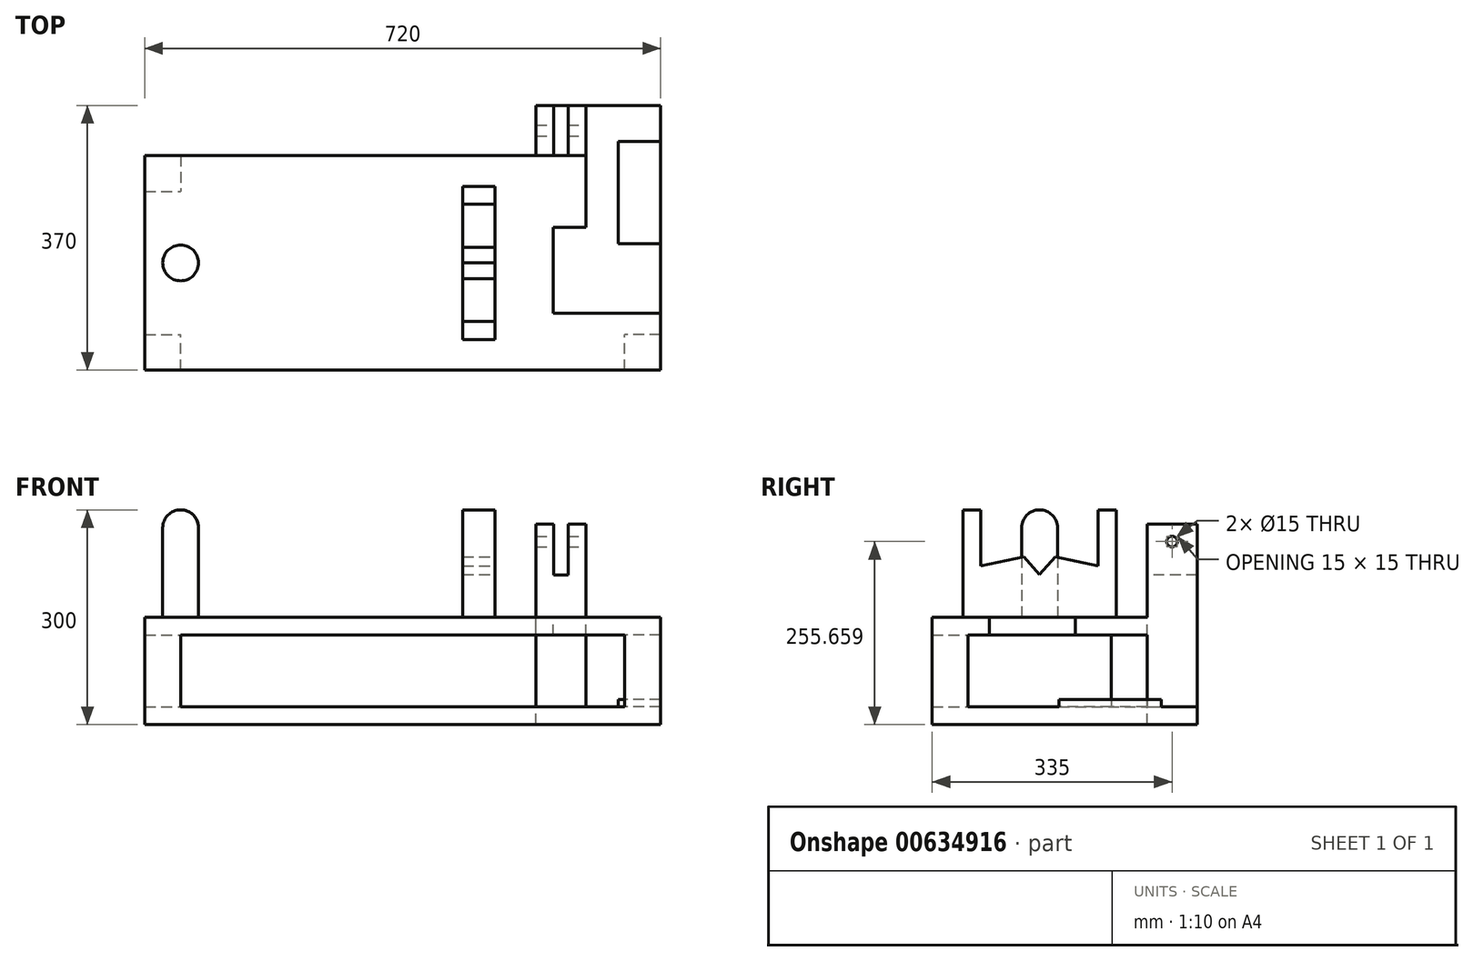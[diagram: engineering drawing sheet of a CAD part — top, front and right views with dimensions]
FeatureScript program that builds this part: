
annotation { "Feature Type Name" : "Feature", "Feature Type Description" : "" }
export const myFeature = defineFeature(function(context is Context, id is Id, definition is map)
    precondition{}
    {
        {
            var Q0;
            Q0=qCreatedBy(makeId("Top.planeOp"),FACE);
            var sketch = newSketch(context, id + "F0", { "sketchPlane" : qUnion([Q0])});
            skLineSegment(sketch, "E0.bottom", {"start": v(-360, 150) * mm, "end": v(360, 150) * mm});
            skLineSegment(sketch, "E0.top", {"start": v(-360, -150) * mm, "end": v(360, -150) * mm});
            skLineSegment(sketch, "E0.left", {"start": v(-360, 150) * mm, "end": v(-360, -150) * mm});
            skLineSegment(sketch, "E0.right", {"start": v(360, 150) * mm, "end": v(360, -150) * mm});
            skSolve(sketch);
        }
        {
            var Q0;
            Q0=makeQuery(id+"F0.imprint","IMPRINT",FACE,{"disambiguationData":[TD([[makeQuery(id+"F0.imprint","IMPRINT",EDGE,{"derivedFrom":sQuery(id+"F0.wireOp",EDGE,"E0.bottom")}),-1.0]])]});
            extrude(context, id + "F1", {"entities" : qUnion([Q0]), "depth" : 25 * mm, "offsetDistance" : 25 * mm});
        }
        {
            var Q0;
            Q0=makeQuery(id+"F1.opExtrude","CAP_FACE",FACE,{"disambiguationData":[OSD([sQuery(id+"F0.wireOp",EDGE,"E0.bottom"),sQuery(id+"F0.wireOp",EDGE,"E0.top"),sQuery(id+"F0.wireOp",EDGE,"E0.left"),sQuery(id+"F0.wireOp",EDGE,"E0.right")])],"isStart":false});
            var sketch = newSketch(context, id + "F2", { "sketchPlane" : qUnion([Q0])});
            skLineSegment(sketch, "E1.bottom", {"start": v(-360, -150) * mm, "end": v(-310, -150) * mm});
            skLineSegment(sketch, "E1.top", {"start": v(-360, -100) * mm, "end": v(-310, -100) * mm});
            skLineSegment(sketch, "E1.left", {"start": v(-360, -150) * mm, "end": v(-360, -100) * mm});
            skLineSegment(sketch, "E1.right", {"start": v(-310, -150) * mm, "end": v(-310, -100) * mm});
            skSolve(sketch);
        }
        {
            var Q0;
            Q0=makeQuery(id+"F2.imprint","IMPRINT",FACE,{"disambiguationData":[TD([[makeQuery(id+"F2.imprint","IMPRINT",EDGE,{"derivedFrom":sQuery(id+"F2.wireOp",EDGE,"E1.bottom")}),1.0]])]});
            extrude(context, id + "F3", {"entities" : qUnion([Q0]), "operationType" : NewBodyOperationType.ADD, "depth" : 100 * mm, "offsetDistance" : 25 * mm});
        }
        {
            var Q0;
            Q0=makeQuery(id+"F1.opExtrude","CAP_FACE",FACE,{"disambiguationData":[OSD([sQuery(id+"F0.wireOp",EDGE,"E0.bottom"),sQuery(id+"F0.wireOp",EDGE,"E0.top"),sQuery(id+"F0.wireOp",EDGE,"E0.left"),sQuery(id+"F0.wireOp",EDGE,"E0.right")])],"isStart":false});
            var sketch = newSketch(context, id + "F4", { "sketchPlane" : qUnion([Q0])});
            skLineSegment(sketch, "E2.bottom", {"start": v(360, -150) * mm, "end": v(310, -150) * mm});
            skLineSegment(sketch, "E2.top", {"start": v(360, -100) * mm, "end": v(310, -100) * mm});
            skLineSegment(sketch, "E2.left", {"start": v(360, -150) * mm, "end": v(360, -100) * mm});
            skLineSegment(sketch, "E2.right", {"start": v(310, -150) * mm, "end": v(310, -100) * mm});
            skLineSegment(sketch, "E3.bottom", {"start": v(360, 150) * mm, "end": v(310, 150) * mm});
            skLineSegment(sketch, "E3.top", {"start": v(360, 100) * mm, "end": v(310, 100) * mm});
            skLineSegment(sketch, "E3.left", {"start": v(360, 150) * mm, "end": v(360, 100) * mm});
            skLineSegment(sketch, "E3.right", {"start": v(310, 150) * mm, "end": v(310, 100) * mm});
            skLineSegment(sketch, "E4.bottom", {"start": v(-360, 150) * mm, "end": v(-310, 150) * mm});
            skLineSegment(sketch, "E4.top", {"start": v(-360, 100) * mm, "end": v(-310, 100) * mm});
            skLineSegment(sketch, "E4.left", {"start": v(-360, 150) * mm, "end": v(-360, 100) * mm});
            skLineSegment(sketch, "E4.right", {"start": v(-310, 150) * mm, "end": v(-310, 100) * mm});
            skSolve(sketch);
        }
        {
            var Q0;
            Q0=makeQuery(id+"F4.imprint","IMPRINT",FACE,{"disambiguationData":[TD([[makeQuery(id+"F4.imprint","IMPRINT",EDGE,{"derivedFrom":sQuery(id+"F4.wireOp",EDGE,"E2.bottom")}),1.0]])]});
            var Q1;
            Q1=makeQuery(id+"F4.imprint","IMPRINT",FACE,{"disambiguationData":[TD([[makeQuery(id+"F4.imprint","IMPRINT",EDGE,{"derivedFrom":sQuery(id+"F4.wireOp",EDGE,"E4.bottom")}),-1.0]])]});
            var Q2;
            Q2=makeQuery(id+"F4.imprint","IMPRINT",FACE,{"disambiguationData":[TD([[makeQuery(id+"F4.imprint","IMPRINT",EDGE,{"derivedFrom":sQuery(id+"F4.wireOp",EDGE,"E3.bottom")}),-1.0]])]});
            extrude(context, id + "F5", {"entities" : qUnion([Q0, Q1, Q2]), "operationType" : NewBodyOperationType.ADD, "depth" : 100 * mm, "offsetDistance" : 25 * mm});
        }
        {
            var Q0;
            Q0=makeQuery(id+"F5.opExtrude","CAP_FACE",FACE,{"disambiguationData":[OSD([sQuery(id+"F4.wireOp",EDGE,"E4.bottom"),sQuery(id+"F4.wireOp",EDGE,"E4.top"),sQuery(id+"F4.wireOp",EDGE,"E4.left"),sQuery(id+"F4.wireOp",EDGE,"E4.right")])],"isStart":false});
            var sketch = newSketch(context, id + "F6", { "sketchPlane" : qUnion([Q0])});
            skLineSegment(sketch, "E5.bottom", {"start": v(-360, 150) * mm, "end": v(360, 150) * mm});
            skLineSegment(sketch, "E5.top", {"start": v(-360, -150) * mm, "end": v(360, -150) * mm});
            skLineSegment(sketch, "E5.left", {"start": v(-360, 150) * mm, "end": v(-360, -150) * mm});
            skLineSegment(sketch, "E5.right", {"start": v(360, 150) * mm, "end": v(360, -150) * mm});
            skSolve(sketch);
        }
        {
            var Q0;
            {var subQ4=makeQuery(id+"F5.opExtrude","CAP_EDGE",EDGE,{"disambiguationData":[OSD([sQuery(id+"F4.wireOp",EDGE,"E4.top")])],"isStart":false});Q0=makeQuery(id+"F6.imprint","IMPRINT",FACE,{"disambiguationData":[TD([[makeQuery(id+"F6.imprint","IMPRINT",EDGE,{"derivedFrom":subQ4}),1.0]])]});}
            var Q1;
            {var subQ3=sQuery(id+"F6.wireOp",EDGE,"E5.top");Q1=makeQuery(id+"F6.imprint","IMPRINT",FACE,{"disambiguationData":[TD([[makeQuery(id+"F6.imprint","IMPRINT",EDGE,{"derivedFrom":subQ3}),1.0]])]});}
            extrude(context, id + "F7", {"entities" : qUnion([Q0, Q1]), "operationType" : NewBodyOperationType.ADD, "depth" : 25 * mm, "offsetDistance" : 25 * mm});
        }
        {
            var Q0;
            Q0=makeQuery(id+"F7.opExtrude","CAP_FACE",FACE,{"disambiguationData":[OSD([sQuery(id+"F6.wireOp",EDGE,"E5.bottom"),sQuery(id+"F6.wireOp",EDGE,"E5.top"),sQuery(id+"F6.wireOp",EDGE,"E5.left"),sQuery(id+"F6.wireOp",EDGE,"E5.right")])],"isStart":false});
            var sketch = newSketch(context, id + "F8", { "sketchPlane" : qUnion([Q0])});
            skCircle(sketch, "E6", {"center": v(-310, 0) * mm, "radius": 25 * mm});
            skSolve(sketch);
        }
        {
            var Q0;
            Q0=makeQuery(id+"F8.imprint","IMPRINT",FACE,{"disambiguationData":[TD([[makeQuery(id+"F8.imprint","IMPRINT",EDGE,{"derivedFrom":sQuery(id+"F8.wireOp",EDGE,"E6")}),1.0]])]});
            extrude(context, id + "F9", {"entities" : qUnion([Q0]), "operationType" : NewBodyOperationType.ADD, "depth" : 150 * mm, "offsetDistance" : 25 * mm});
        }
        {
            var Q0;
            Q0=makeQuery(id+"F7.opExtrude","CAP_FACE",FACE,{"disambiguationData":[OSD([sQuery(id+"F6.wireOp",EDGE,"E5.bottom"),sQuery(id+"F6.wireOp",EDGE,"E5.top"),sQuery(id+"F6.wireOp",EDGE,"E5.left"),sQuery(id+"F6.wireOp",EDGE,"E5.right")])],"isStart":false});
            var sketch = newSketch(context, id + "F10", { "sketchPlane" : qUnion([Q0])});
            skLineSegment(sketch, "E7.bottom", {"start": v(84, 106.83) * mm, "end": v(129, 106.83) * mm});
            skLineSegment(sketch, "E7.top", {"start": v(84, -106.83) * mm, "end": v(129, -106.83) * mm});
            skLineSegment(sketch, "E7.left", {"start": v(84, 106.83) * mm, "end": v(84, -106.83) * mm});
            skLineSegment(sketch, "E7.right", {"start": v(129, 106.83) * mm, "end": v(129, -106.83) * mm});
            skLineSegment(sketch, "E8", {"start": v(-360, 0) * mm, "end": v(360, 0) * mm});
            skSolve(sketch);
        }
        {
            var Q0;
            {var subQ0=sQuery(id+"F10.wireOp",EDGE,"E7.top");Q0=makeQuery(id+"F10.imprint","IMPRINT",FACE,{"disambiguationData":[TD([[makeQuery(id+"F10.imprint","IMPRINT",EDGE,{"derivedFrom":subQ0}),1.0]])]});}
            var Q1;
            {var subQ0=sQuery(id+"F10.wireOp",EDGE,"E7.bottom");Q1=makeQuery(id+"F10.imprint","IMPRINT",FACE,{"disambiguationData":[TD([[makeQuery(id+"F10.imprint","IMPRINT",EDGE,{"derivedFrom":subQ0}),-1.0]])]});}
            extrude(context, id + "F11", {"entities" : qUnion([Q0, Q1]), "operationType" : NewBodyOperationType.ADD, "depth" : 150 * mm, "offsetDistance" : 25 * mm});
        }
        {
            var Q0;
            Q0=makeQuery(id+"F11.opExtrude","SWEPT_FACE",FACE,{"disambiguationData":[OSD([sQuery(id+"F10.wireOp",EDGE,"E7.right")])]});
            var sketch = newSketch(context, id + "F12", { "sketchPlane" : qUnion([Q0])});
            skLineSegment(sketch, "E9", {"start": v(-81.83, 300) * mm, "end": v(-81.83, 221.94) * mm});
            skLineSegment(sketch, "E10", {"start": v(-81.83, 221.94) * mm, "end": v(-21.83, 234.49) * mm});
            skLineSegment(sketch, "E11", {"start": v(-21.83, 234.49) * mm, "end": v(0, 209.4) * mm});
            skLineSegment(sketch, "E12", {"start": v(0, 209.4) * mm, "end": v(21.83, 234.49) * mm});
            skLineSegment(sketch, "E13", {"start": v(21.83, 234.49) * mm, "end": v(81.83, 221.94) * mm});
            skLineSegment(sketch, "E14", {"start": v(81.83, 221.94) * mm, "end": v(81.83, 300) * mm});
            skLineSegment(sketch, "E15", {"start": v(-81.83, 300) * mm, "end": v(81.83, 300) * mm});
            skSolve(sketch);
        }
        {
            var Q0;
            Q0=qSketchRegion(id+"F12",true);
            extrude(context, id + "F13", {"entities" : qUnion([Q0]), "operationType" : NewBodyOperationType.REMOVE, "oppositeDirection" : true, "depth" : 50 * mm, "offsetDistance" : 25 * mm});
        }
        {
            var Q0;
            Q0=makeQuery(id+"F7.opExtrude","CAP_FACE",FACE,{"disambiguationData":[OSD([sQuery(id+"F6.wireOp",EDGE,"E5.bottom"),sQuery(id+"F6.wireOp",EDGE,"E5.top"),sQuery(id+"F6.wireOp",EDGE,"E5.left"),sQuery(id+"F6.wireOp",EDGE,"E5.right")])],"isStart":false});
            var sketch = newSketch(context, id + "F14", { "sketchPlane" : qUnion([Q0])});
            skLineSegment(sketch, "E16.bottom", {"start": v(186, 150) * mm, "end": v(256, 150) * mm});
            skLineSegment(sketch, "E16.top", {"start": v(186, 220) * mm, "end": v(256, 220) * mm});
            skLineSegment(sketch, "E16.left", {"start": v(186, 150) * mm, "end": v(186, 220) * mm});
            skLineSegment(sketch, "E16.right", {"start": v(256, 150) * mm, "end": v(256, 220) * mm});
            skSolve(sketch);
        }
        {
            var Q0;
            Q0=qSketchRegion(id+"F14",true);
            extrude(context, id + "F15", {"entities" : qUnion([Q0]), "operationType" : NewBodyOperationType.ADD, "oppositeDirection" : true, "depth" : 150 * mm, "offsetDistance" : 25 * mm});
        }
        {
            var Q0;
            Q0=qSketchRegion(id+"F14",true);
            extrude(context, id + "F16", {"entities" : qUnion([Q0]), "operationType" : NewBodyOperationType.ADD, "depth" : 130 * mm, "offsetDistance" : 25 * mm});
        }
        {
            var Q0;
            Q0=makeQuery(id+"F9.opExtrude","CAP_FACE",FACE,{"disambiguationData":[OSD([sQuery(id+"F8.wireOp",EDGE,"E6")])],"isStart":false});
            fillet(context, id + "F17", {"entities" : qUnion([Q0]), "radius" : 25 * mm, "tangentPropagation" : true, "allowEdgeOverflow" : false});
        }
        {
            var Q0;
            Q0=makeQuery(id+"F15.boolean.opBoolean","MERGE",FACE,{"derivedFrom":[makeQuery(id+"F7.opExtrude","CAP_FACE",FACE,{"disambiguationData":[OSD([sQuery(id+"F6.wireOp",EDGE,"E5.bottom"),sQuery(id+"F6.wireOp",EDGE,"E5.top"),sQuery(id+"F6.wireOp",EDGE,"E5.left"),sQuery(id+"F6.wireOp",EDGE,"E5.right")])],"isStart":false}),makeQuery(id+"F15.opExtrude","CAP_FACE",FACE,{"disambiguationData":[OSD([sQuery(id+"F14.wireOp",EDGE,"E16.bottom"),sQuery(id+"F14.wireOp",EDGE,"E16.top"),sQuery(id+"F14.wireOp",EDGE,"E16.left"),sQuery(id+"F14.wireOp",EDGE,"E16.right")])],"isStart":true})]});
            var sketch = newSketch(context, id + "F18", { "sketchPlane" : qUnion([Q0])});
            skLineSegment(sketch, "E17.bottom", {"start": v(360, -70) * mm, "end": v(210, -70) * mm});
            skLineSegment(sketch, "E17.top", {"start": v(360, 50) * mm, "end": v(210, 50) * mm});
            skLineSegment(sketch, "E17.left", {"start": v(360, -70) * mm, "end": v(360, 50) * mm});
            skLineSegment(sketch, "E17.right", {"start": v(210, -70) * mm, "end": v(210, 50) * mm});
            skSolve(sketch);
        }
        {
            var Q0;
            Q0=qSketchRegion(id+"F18",true);
            extrude(context, id + "F19", {"entities" : qUnion([Q0]), "operationType" : NewBodyOperationType.REMOVE, "oppositeDirection" : true, "depth" : 25 * mm, "offsetDistance" : 25 * mm});
        }
        {
            var Q0;
            Q0=makeQuery(id+"F15.boolean.opBoolean","MERGE",FACE,{"derivedFrom":[makeQuery(id+"F7.opExtrude","CAP_FACE",FACE,{"disambiguationData":[OSD([sQuery(id+"F6.wireOp",EDGE,"E5.bottom"),sQuery(id+"F6.wireOp",EDGE,"E5.top"),sQuery(id+"F6.wireOp",EDGE,"E5.left"),sQuery(id+"F6.wireOp",EDGE,"E5.right")])],"isStart":false}),makeQuery(id+"F15.opExtrude","CAP_FACE",FACE,{"disambiguationData":[OSD([sQuery(id+"F14.wireOp",EDGE,"E16.bottom"),sQuery(id+"F14.wireOp",EDGE,"E16.top"),sQuery(id+"F14.wireOp",EDGE,"E16.left"),sQuery(id+"F14.wireOp",EDGE,"E16.right")])],"isStart":true})]});
            var sketch = newSketch(context, id + "F20", { "sketchPlane" : qUnion([Q0])});
            skLineSegment(sketch, "E18.bottom", {"start": v(360, 150) * mm, "end": v(256, 150) * mm});
            skLineSegment(sketch, "E18.top", {"start": v(360, 50) * mm, "end": v(256, 50) * mm});
            skLineSegment(sketch, "E18.left", {"start": v(360, 150) * mm, "end": v(360, 50) * mm});
            skLineSegment(sketch, "E18.right", {"start": v(256, 150) * mm, "end": v(256, 50) * mm});
            skSolve(sketch);
        }
        {
            var Q0;
            Q0=qSketchRegion(id+"F20",true);
            extrude(context, id + "F21", {"entities" : qUnion([Q0]), "operationType" : NewBodyOperationType.REMOVE, "oppositeDirection" : true, "depth" : 150 * mm, "offsetDistance" : 25 * mm});
        }
        {
            var Q0;
            Q0=makeQuery(id+"F1.opExtrude","CAP_FACE",FACE,{"disambiguationData":[OSD([sQuery(id+"F0.wireOp",EDGE,"E0.bottom"),sQuery(id+"F0.wireOp",EDGE,"E0.top"),sQuery(id+"F0.wireOp",EDGE,"E0.left"),sQuery(id+"F0.wireOp",EDGE,"E0.right")])],"isStart":false});
            var sketch = newSketch(context, id + "F22", { "sketchPlane" : qUnion([Q0])});
            skLineSegment(sketch, "E19.bottom", {"start": v(360, 50) * mm, "end": v(256, 50) * mm});
            skLineSegment(sketch, "E19.top", {"start": v(360, 220) * mm, "end": v(256, 220) * mm});
            skLineSegment(sketch, "E19.left", {"start": v(360, 50) * mm, "end": v(360, 220) * mm});
            skLineSegment(sketch, "E19.right", {"start": v(256, 50) * mm, "end": v(256, 220) * mm});
            skSolve(sketch);
        }
        {
            var Q0;
            Q0=qSketchRegion(id+"F22",true);
            extrude(context, id + "F23", {"entities" : qUnion([Q0]), "operationType" : NewBodyOperationType.ADD, "oppositeDirection" : true, "depth" : 25 * mm, "offsetDistance" : 25 * mm});
        }
        {
            var Q0;
            Q0=makeQuery(id+"F16.opExtrude","SWEPT_FACE",FACE,{"disambiguationData":[OSD([sQuery(id+"F14.wireOp",EDGE,"E16.bottom")])]});
            var sketch = newSketch(context, id + "F24", { "sketchPlane" : qUnion([Q0])});
            skLineSegment(sketch, "E20.bottom", {"start": v(211, 280) * mm, "end": v(231, 280) * mm});
            skLineSegment(sketch, "E20.top", {"start": v(211, 208.66) * mm, "end": v(231, 208.66) * mm});
            skLineSegment(sketch, "E20.left", {"start": v(211, 280) * mm, "end": v(211, 208.66) * mm});
            skLineSegment(sketch, "E20.right", {"start": v(231, 280) * mm, "end": v(231, 208.66) * mm});
            skSolve(sketch);
        }
        {
            var Q0;
            Q0 = qSketchRegion(id + "F24", true);
            extrude(context, id + "F25", {"entities" : qUnion([Q0]), "operationType" : NewBodyOperationType.REMOVE, "oppositeDirection" : true, "depth" : 80 * mm, "offsetDistance" : 25 * mm});
        }
        {
            var Q0;
            {var subQ0=sQuery(id+"F14.wireOp",EDGE,"E16.right");Q0=makeQuery(id+"F21.boolean.opBoolean","MERGE",FACE,{"derivedFrom":[makeQuery(id+"F16.boolean.opBoolean","MERGE",FACE,{"derivedFrom":[makeQuery(id+"F15.opExtrude","SWEPT_FACE",FACE,{"disambiguationData":[OSD([subQ0])]}),makeQuery(id+"F16.opExtrude","SWEPT_FACE",FACE,{"disambiguationData":[OSD([subQ0])]})]}),makeQuery(id+"F21.opExtrude","SWEPT_FACE",FACE,{"disambiguationData":[OSD([sQuery(id+"F20.wireOp",EDGE,"E18.right")])]})]});}
            var sketch = newSketch(context, id + "F26", { "sketchPlane" : qUnion([Q0])});
            skCircle(sketch, "E21", {"center": v(185, 255.66) * mm, "radius": 7.5 * mm});
            skPoint(sketch, "E21.centerSnap0", {"position": v(185, 280) * mm});
            skSolve(sketch);
        }
        {
            var Q0;
            Q0 = qSketchRegion(id + "F26", true);
            extrude(context, id + "F27", {"entities" : qUnion([Q0]), "operationType" : NewBodyOperationType.REMOVE, "endBound" : BoundingType.THROUGH_ALL, "oppositeDirection" : true, "depth" : 25 * mm, "offsetDistance" : 25 * mm});
        }
        {
            var Q0;
            Q0=makeQuery(id+"F23.boolean.opBoolean","MERGE",FACE,{"derivedFrom":[makeQuery(id+"F1.opExtrude","CAP_FACE",FACE,{"disambiguationData":[OSD([sQuery(id+"F0.wireOp",EDGE,"E0.bottom"),sQuery(id+"F0.wireOp",EDGE,"E0.top"),sQuery(id+"F0.wireOp",EDGE,"E0.left"),sQuery(id+"F0.wireOp",EDGE,"E0.right")])],"isStart":false}),makeQuery(id+"F23.opExtrude","CAP_FACE",FACE,{"disambiguationData":[OSD([sQuery(id+"F22.wireOp",EDGE,"E19.bottom"),sQuery(id+"F22.wireOp",EDGE,"E19.top"),sQuery(id+"F22.wireOp",EDGE,"E19.left"),sQuery(id+"F22.wireOp",EDGE,"E19.right")])],"isStart":true})]});
            var sketch = newSketch(context, id + "F28", { "sketchPlane" : qUnion([Q0])});
            skLineSegment(sketch, "E22.bottom", {"start": v(360, 27) * mm, "end": v(301.21, 27) * mm});
            skLineSegment(sketch, "E22.top", {"start": v(360, 170) * mm, "end": v(301.21, 170) * mm});
            skLineSegment(sketch, "E22.left", {"start": v(360, 27) * mm, "end": v(360, 170) * mm});
            skLineSegment(sketch, "E22.right", {"start": v(301.21, 27) * mm, "end": v(301.21, 170) * mm});
            skSolve(sketch);
        }
        {
            var Q0;
            Q0 = qSketchRegion(id + "F28", true);
            extrude(context, id + "F29", {"entities" : qUnion([Q0]), "operationType" : NewBodyOperationType.ADD, "depth" : 10 * mm, "offsetDistance" : 25 * mm});
        }
    });
